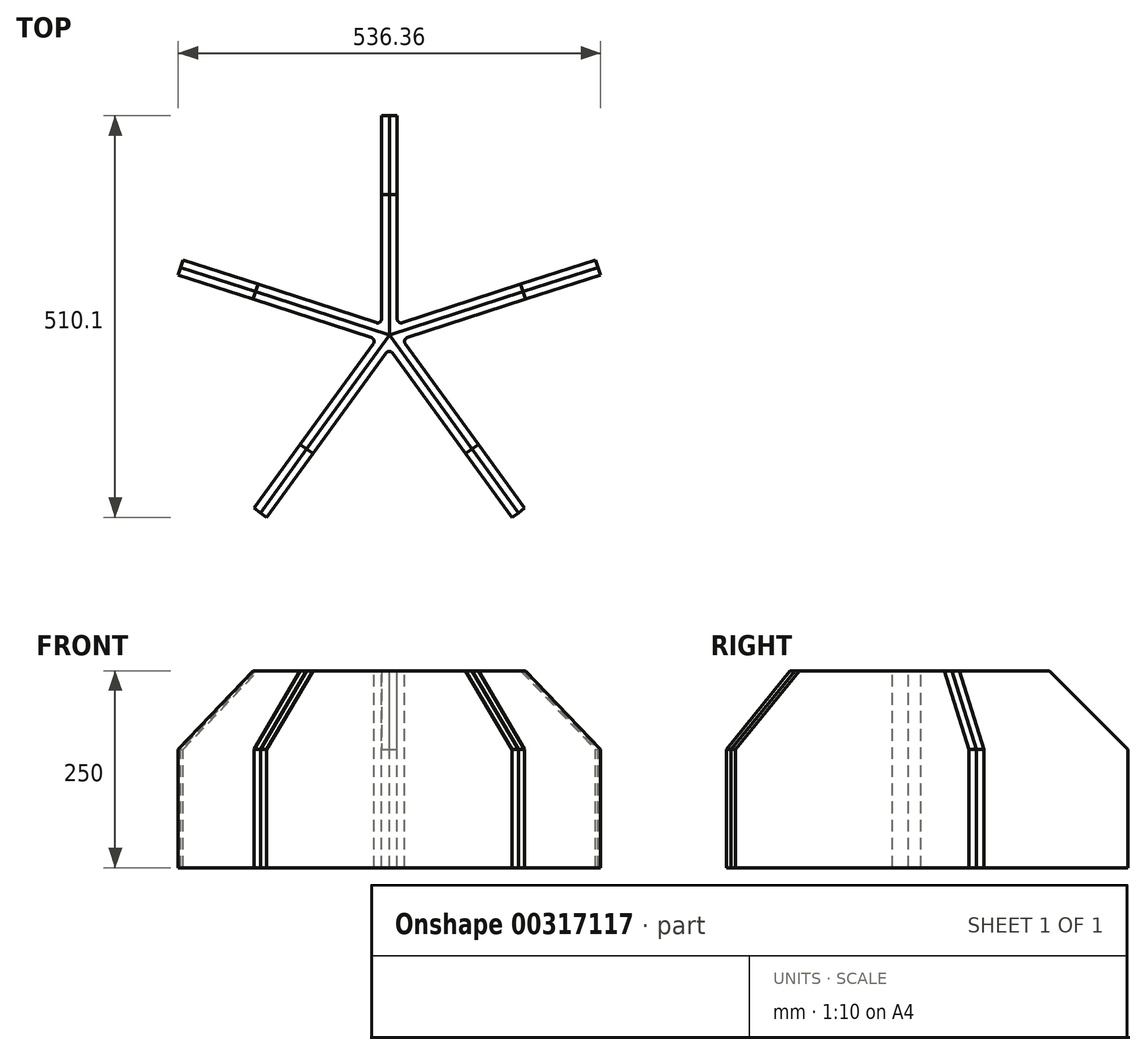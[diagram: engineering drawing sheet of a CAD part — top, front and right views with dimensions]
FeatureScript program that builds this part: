
annotation { "Feature Type Name" : "Feature", "Feature Type Description" : "" }
export const myFeature = defineFeature(function(context is Context, id is Id, definition is map)
    precondition{}
    {
        {
            var Q0;
            Q0=qCreatedBy(makeId("Top.planeOp"),FACE);
            cPlane(context, id + "F0", {"entities" : qUnion([Q0]), "cplaneType" : CPlaneType.OFFSET, "offset" : 25 * mm, "width" : 150 * mm, "height" : 150 * mm});
        }
        {
            var Q0;
            Q0=qCreatedBy(id+"F0.planeOp",FACE);
            var sketch = newSketch(context, id + "F1", { "sketchPlane" : qUnion([Q0])});
            skCircle(sketch, "E0.cCircle", {"center": v(-14.87, -3.4) * mm, "radius": 240.87 * mm, "construction": true});
            skPoint(sketch, "E0.0.midPoint", {"position": v(132.77, 179.2) * mm});
            skLineSegment(sketch, "E1", {"start": v(0, 0) * mm, "end": v(283.16, 92) * mm});
            skLineSegment(sketch, "E2", {"start": v(0, 0) * mm, "end": v(175, -240.87) * mm});
            skLineSegment(sketch, "E3.0", {"start": v(22.73, -3.13) * mm, "end": v(286.25, 82.5) * mm});
            skLineSegment(sketch, "E3.1", {"start": v(20.23, -10.82) * mm, "end": v(183.1, -234.99) * mm});
            skLineSegment(sketch, "E4", {"start": v(283.16, 92) * mm, "end": v(286.25, 82.5) * mm, "construction": true});
            skLineSegment(sketch, "E5", {"start": v(183.1, -234.99) * mm, "end": v(175, -240.87) * mm, "construction": true});
            skPoint(sketch, "E6.visualSharp", {"position": v(7.37, -20.92) * mm});
            skArc(sketch, "E6.filletArc", {"start": v(22.73, -3.13) * mm, "mid": v(19.52, -6.34) * mm, "end": v(20.23, -10.82) * mm});
            skLineSegment(sketch, "E7.0", {"start": v(171.92, -219.62) * mm, "end": v(163.83, -225.5) * mm});
            skLineSegment(sketch, "E8.0", {"start": v(265.09, 86.13) * mm, "end": v(268.18, 76.62) * mm});
            skSolve(sketch);
        }
        {
            var Q0;
            Q0 = qSketchRegion(id + "F1", true);
            extrude(context, id + "F2", {"entities" : qUnion([Q0]), "oppositeDirection" : true, "depth" : 250 * mm});
        }
        {
            var Q0;
            Q0=makeQuery(id+"F2.opExtrude","SWEPT_BODY",BODY,{"disambiguationData":[OSD([sQuery(id+"F1.wireOp",EDGE,"E1"),sQuery(id+"F1.wireOp",EDGE,"E2"),sQuery(id+"F1.wireOp",EDGE,"E3.0"),sQuery(id+"F1.wireOp",EDGE,"E3.1"),sQuery(id+"F1.wireOp",EDGE,"E4"),sQuery(id+"F1.wireOp",EDGE,"E5"),sQuery(id+"F1.wireOp",EDGE,"E6.filletArc")])]});
            var Q1;
            Q1=makeQuery(id+"F2.opExtrude","SWEPT_EDGE",EDGE,{"disambiguationData":[OSD([sQuery(id+"F1.wireOp",EDGE,"E1"),sQuery(id+"F1.wireOp",EDGE,"E2")])]});
            circularPattern(context, id + "F3", {"entities" : qUnion([Q0]), "axis" : qUnion([Q1]), "angle" : 360 * degree, "instanceCount" : 5, "equalSpace" : true});
        }
        {
            var Q0;
            Q0=makeQuery(id+"F2.opExtrude","CAP_EDGE",EDGE,{"disambiguationData":[OSD([sQuery(id+"F1.wireOp",EDGE,"E4")])],"isStart":true});
            var Q1;
            Q1=makeQuery(id+"F2.opExtrude","CAP_EDGE",EDGE,{"disambiguationData":[OSD([sQuery(id+"F1.wireOp",EDGE,"E5")])],"isStart":true});
            var Q2;
            Q2=makeQuery(id+"F3.opPattern","COPY",EDGE,{"derivedFrom":makeQuery(id+"F2.opExtrude","CAP_EDGE",EDGE,{"disambiguationData":[OSD([sQuery(id+"F1.wireOp",EDGE,"E4")])],"isStart":true}),"instanceName":"4"});
            var Q3;
            Q3=makeQuery(id+"F3.opPattern","COPY",EDGE,{"derivedFrom":makeQuery(id+"F2.opExtrude","CAP_EDGE",EDGE,{"disambiguationData":[OSD([sQuery(id+"F1.wireOp",EDGE,"E4")])],"isStart":true}),"instanceName":"3"});
            var Q4;
            Q4=makeQuery(id+"F3.opPattern","COPY",EDGE,{"derivedFrom":makeQuery(id+"F2.opExtrude","CAP_EDGE",EDGE,{"disambiguationData":[OSD([sQuery(id+"F1.wireOp",EDGE,"E5")])],"isStart":true}),"instanceName":"4"});
            var Q5;
            Q5=makeQuery(id+"F3.opPattern","COPY",EDGE,{"derivedFrom":makeQuery(id+"F2.opExtrude","CAP_EDGE",EDGE,{"disambiguationData":[OSD([sQuery(id+"F1.wireOp",EDGE,"E5")])],"isStart":true}),"instanceName":"3"});
            var Q6;
            Q6=makeQuery(id+"F3.opPattern","COPY",EDGE,{"derivedFrom":makeQuery(id+"F2.opExtrude","CAP_EDGE",EDGE,{"disambiguationData":[OSD([sQuery(id+"F1.wireOp",EDGE,"E4")])],"isStart":true}),"instanceName":"2"});
            var Q7;
            Q7=makeQuery(id+"F3.opPattern","COPY",EDGE,{"derivedFrom":makeQuery(id+"F2.opExtrude","CAP_EDGE",EDGE,{"disambiguationData":[OSD([sQuery(id+"F1.wireOp",EDGE,"E4")])],"isStart":true}),"instanceName":"1"});
            var Q8;
            Q8=makeQuery(id+"F3.opPattern","COPY",EDGE,{"derivedFrom":makeQuery(id+"F2.opExtrude","CAP_EDGE",EDGE,{"disambiguationData":[OSD([sQuery(id+"F1.wireOp",EDGE,"E5")])],"isStart":true}),"instanceName":"2"});
            var Q9;
            Q9=makeQuery(id+"F3.opPattern","COPY",EDGE,{"derivedFrom":makeQuery(id+"F2.opExtrude","CAP_EDGE",EDGE,{"disambiguationData":[OSD([sQuery(id+"F1.wireOp",EDGE,"E5")])],"isStart":true}),"instanceName":"1"});
            var Q10;
            Q10=makeQuery(id+"F2.opExtrude","CAP_EDGE",EDGE,{"disambiguationData":[OSD([sQuery(id+"F1.wireOp",EDGE,"E7.0")])],"isStart":true});
            var Q11;
            Q11=makeQuery(id+"F3.opPattern","COPY",EDGE,{"derivedFrom":makeQuery(id+"F2.opExtrude","CAP_EDGE",EDGE,{"disambiguationData":[OSD([sQuery(id+"F1.wireOp",EDGE,"E8.0")])],"isStart":true}),"instanceName":"4"});
            var Q12;
            Q12=makeQuery(id+"F3.opPattern","COPY",EDGE,{"derivedFrom":makeQuery(id+"F2.opExtrude","CAP_EDGE",EDGE,{"disambiguationData":[OSD([sQuery(id+"F1.wireOp",EDGE,"E7.0")])],"isStart":true}),"instanceName":"1"});
            var Q13;
            Q13=makeQuery(id+"F2.opExtrude","CAP_EDGE",EDGE,{"disambiguationData":[OSD([sQuery(id+"F1.wireOp",EDGE,"E8.0")])],"isStart":true});
            var Q14;
            Q14=makeQuery(id+"F3.opPattern","COPY",EDGE,{"derivedFrom":makeQuery(id+"F2.opExtrude","CAP_EDGE",EDGE,{"disambiguationData":[OSD([sQuery(id+"F1.wireOp",EDGE,"E8.0")])],"isStart":true}),"instanceName":"1"});
            var Q15;
            Q15=makeQuery(id+"F3.opPattern","COPY",EDGE,{"derivedFrom":makeQuery(id+"F2.opExtrude","CAP_EDGE",EDGE,{"disambiguationData":[OSD([sQuery(id+"F1.wireOp",EDGE,"E7.0")])],"isStart":true}),"instanceName":"2"});
            var Q16;
            Q16=makeQuery(id+"F3.opPattern","COPY",EDGE,{"derivedFrom":makeQuery(id+"F2.opExtrude","CAP_EDGE",EDGE,{"disambiguationData":[OSD([sQuery(id+"F1.wireOp",EDGE,"E8.0")])],"isStart":true}),"instanceName":"2"});
            var Q17;
            Q17=makeQuery(id+"F3.opPattern","COPY",EDGE,{"derivedFrom":makeQuery(id+"F2.opExtrude","CAP_EDGE",EDGE,{"disambiguationData":[OSD([sQuery(id+"F1.wireOp",EDGE,"E7.0")])],"isStart":true}),"instanceName":"3"});
            var Q18;
            Q18=makeQuery(id+"F3.opPattern","COPY",EDGE,{"derivedFrom":makeQuery(id+"F2.opExtrude","CAP_EDGE",EDGE,{"disambiguationData":[OSD([sQuery(id+"F1.wireOp",EDGE,"E7.0")])],"isStart":true}),"instanceName":"4"});
            var Q19;
            Q19=makeQuery(id+"F3.opPattern","COPY",EDGE,{"derivedFrom":makeQuery(id+"F2.opExtrude","CAP_EDGE",EDGE,{"disambiguationData":[OSD([sQuery(id+"F1.wireOp",EDGE,"E8.0")])],"isStart":true}),"instanceName":"3"});
            chamfer(context, id + "F4", {"entities" : qUnion([Q0, Q1, Q2, Q3, Q4, Q5, Q6, Q7, Q8, Q9, Q10, Q11, Q12, Q13, Q14, Q15, Q16, Q17, Q18, Q19]), "width" : 100 * mm, "tangentPropagation" : true});
        }
    });
